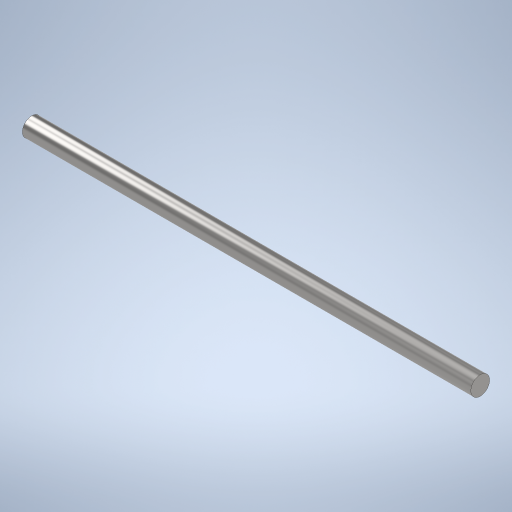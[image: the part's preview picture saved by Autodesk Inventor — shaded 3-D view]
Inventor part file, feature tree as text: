
AUTODESK INVENTOR PART (.ipt)
format: ipt  version: 2024 (Build 280153000, 153)  size: 254,464 bytes
history: native  units: in
note: dims shown in document units (in); Inventor stores cm internally (conversion verified against a paired STEP export)
features: extrude x1, sketch x1
ambient origin geometry x8: Origin, YZ Plane, XZ Plane, XY Plane, X Axis, Y Axis, Z Axis, Center Point
bodies: Solid1 (feature_tree)
feature tree (2):
  extrude  "Extrusion1"  Depth=12.0in TaperAngle=0.0deg
  sketch  "Sketch1"  dims[d0=0.5in d1=12.0in d2=0.0in]
